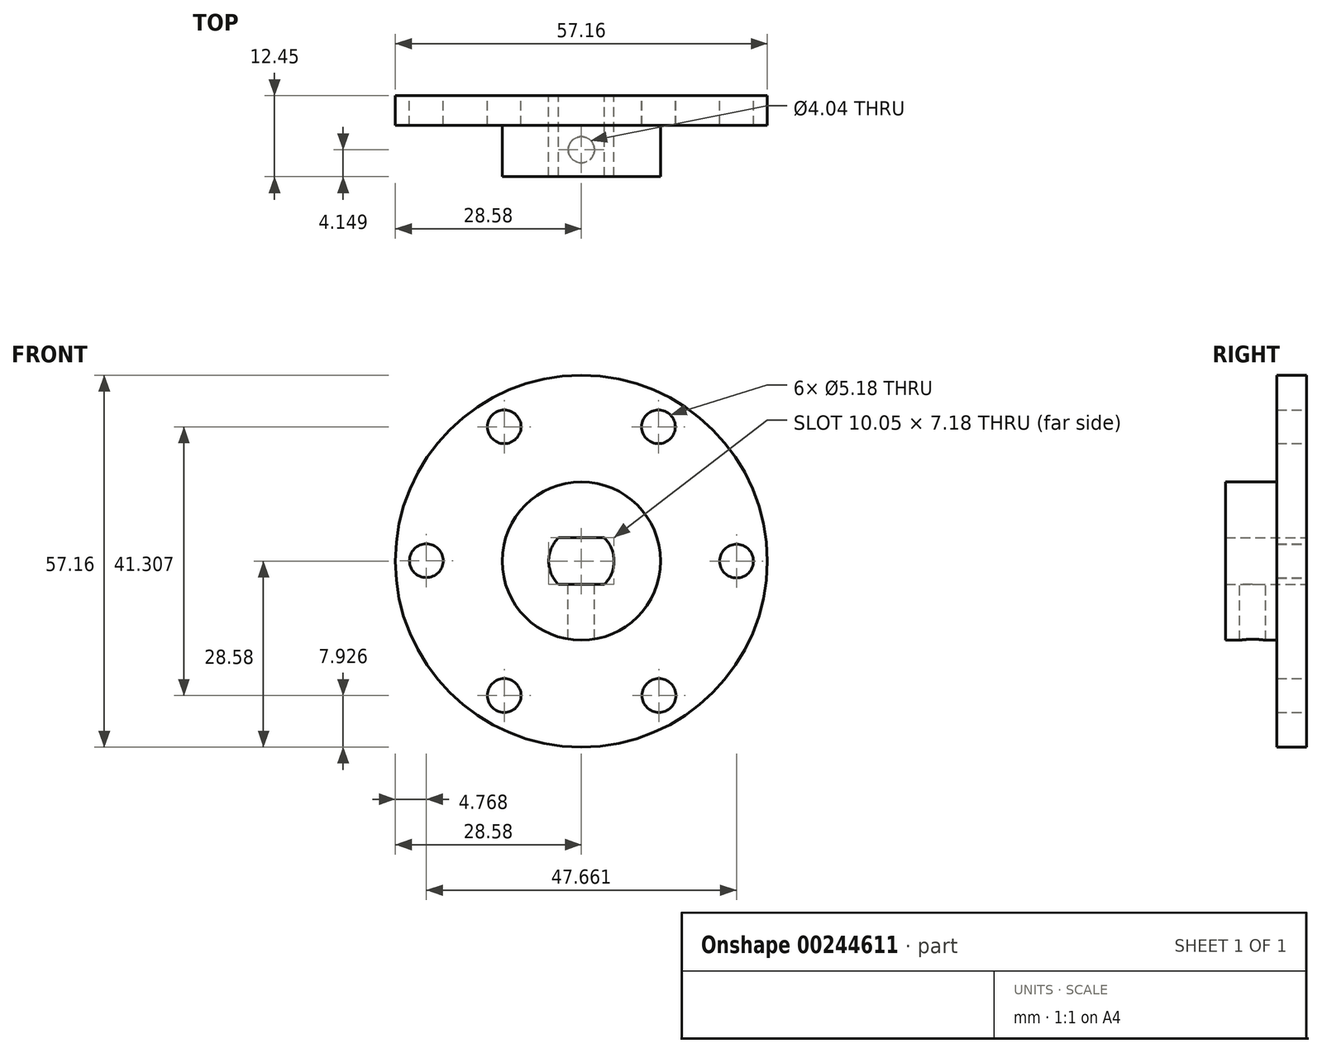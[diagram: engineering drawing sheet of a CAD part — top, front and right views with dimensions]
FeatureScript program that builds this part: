
annotation { "Feature Type Name" : "Feature", "Feature Type Description" : "" }
export const myFeature = defineFeature(function(context is Context, id is Id, definition is map)
    precondition{}
    {
        {
            var Q0;
            Q0=qCreatedBy(makeId("Front.planeOp"),FACE);
            var sketch = newSketch(context, id + "F0", { "sketchPlane" : qUnion([Q0])});
            skCircle(sketch, "E0", {"center": v(0, 0) * mm, "radius": 28.58 * mm});
            skArc(sketch, "E1", {"start": v(-11.85, 20.65) * mm, "mid": v(-11.9, 20.62) * mm, "end": v(-11.96, 20.6) * mm});
            skCircle(sketch, "E2", {"center": v(0, 0) * mm, "radius": 12.17 * mm});
            skLineSegment(sketch, "E3.0", {"start": v(-11.92, 20.65) * mm, "end": v(-11.85, 20.65) * mm});
            skLineSegment(sketch, "E3.1", {"start": v(11.92, 20.65) * mm, "end": v(11.96, 20.6) * mm});
            skLineSegment(sketch, "E3.2", {"start": v(23.85, 0) * mm, "end": v(23.81, -0.06) * mm});
            skLineSegment(sketch, "E3.3", {"start": v(11.92, -20.65) * mm, "end": v(11.85, -20.65) * mm});
            skLineSegment(sketch, "E3.4", {"start": v(-11.92, -20.65) * mm, "end": v(-11.96, -20.6) * mm});
            skLineSegment(sketch, "E3.5", {"start": v(-23.85, 0) * mm, "end": v(-23.81, 0.06) * mm});
            skPoint(sketch, "E3.0.midPoint", {"position": v(0, 20.65) * mm});
            skArc(sketch, "E4.trimOffspring", {"start": v(-23.81, 0.06) * mm, "mid": v(-23.81, 0) * mm, "end": v(-23.81, -0.06) * mm});
            skArc(sketch, "E5.trimOffspring", {"start": v(-11.96, -20.6) * mm, "mid": v(-11.9, -20.62) * mm, "end": v(-11.85, -20.65) * mm});
            skArc(sketch, "E6.trimOffspring", {"start": v(11.85, -20.65) * mm, "mid": v(11.9, -20.62) * mm, "end": v(11.96, -20.6) * mm});
            skArc(sketch, "E7.trimOffspring", {"start": v(23.81, -0.06) * mm, "mid": v(23.81, 0) * mm, "end": v(23.81, 0.06) * mm});
            skArc(sketch, "E8.trimOffspring", {"start": v(11.96, 20.6) * mm, "mid": v(11.9, 20.62) * mm, "end": v(11.85, 20.65) * mm});
            skCircle(sketch, "E9", {"center": v(-23.81, 0.06) * mm, "radius": 2.6 * mm});
            skCircle(sketch, "E10", {"center": v(-11.85, 20.65) * mm, "radius": 2.6 * mm});
            skCircle(sketch, "E11", {"center": v(11.85, 20.65) * mm, "radius": 2.6 * mm});
            skCircle(sketch, "E12", {"center": v(23.85, 0) * mm, "radius": 2.6 * mm});
            skCircle(sketch, "E13", {"center": v(11.92, -20.65) * mm, "radius": 2.6 * mm});
            skCircle(sketch, "E14", {"center": v(-11.85, -20.65) * mm, "radius": 2.6 * mm});
            skLineSegment(sketch, "E15.trimOffspring", {"start": v(11.85, 20.65) * mm, "end": v(11.92, 20.65) * mm});
            skLineSegment(sketch, "E16.trimOffspring", {"start": v(23.81, 0.06) * mm, "end": v(23.85, 0) * mm});
            skLineSegment(sketch, "E17.trimOffspring", {"start": v(11.96, -20.6) * mm, "end": v(11.92, -20.65) * mm});
            skLineSegment(sketch, "E18.trimOffspring", {"start": v(-11.85, -20.65) * mm, "end": v(-11.92, -20.65) * mm});
            skLineSegment(sketch, "E19.trimOffspring", {"start": v(-23.81, -0.06) * mm, "end": v(-23.85, 0) * mm});
            skLineSegment(sketch, "E20.trimOffspring", {"start": v(-11.96, 20.6) * mm, "end": v(-11.92, 20.65) * mm});
            skArc(sketch, "E21", {"start": v(-3.51, 3.6) * mm, "mid": v(-5.02, 0) * mm, "end": v(-3.51, -3.6) * mm});
            skLineSegment(sketch, "E22.bottom", {"start": v(3.51, 3.6) * mm, "end": v(-3.51, 3.6) * mm});
            skLineSegment(sketch, "E22.top", {"start": v(3.51, -3.6) * mm, "end": v(-3.51, -3.6) * mm});
            skArc(sketch, "E23.trimOffspring", {"start": v(3.51, -3.6) * mm, "mid": v(5.02, 0) * mm, "end": v(3.51, 3.6) * mm});
            skSolve(sketch);
        }
        {
            var Q0;
            Q0=makeQuery(id+"F0.imprint","IMPRINT",FACE,{"disambiguationData":[TD([[makeQuery(id+"F0.imprint","IMPRINT",EDGE,{"derivedFrom":sQuery(id+"F0.wireOp",EDGE,"E2")}),1.0]])]});
            extrude(context, id + "F1", {"entities" : qUnion([Q0]), "depth" : 12.45 * mm});
        }
        {
            var Q0;
            Q0=makeQuery(id+"F0.imprint","IMPRINT",FACE,{"disambiguationData":[TD([[makeQuery(id+"F0.imprint","IMPRINT",EDGE,{"derivedFrom":sQuery(id+"F0.wireOp",EDGE,"E0")}),1.0]])]});
            extrude(context, id + "F2", {"entities" : qUnion([Q0]), "operationType" : NewBodyOperationType.ADD, "depth" : 4.57 * mm});
        }
        {
            var Q0;
            Q0=qCreatedBy(makeId("Top.planeOp"),FACE);
            var sketch = newSketch(context, id + "F3", { "sketchPlane" : qUnion([Q0])});
            skCircle(sketch, "E24", {"center": v(0, -8.3) * mm, "radius": 2 * mm});
            skSolve(sketch);
        }
        {
            var Q0;
            Q0=sQuery(id+"F3.wireOp",VERTEX,"E24.center");
            var Q1;
            Q1=makeQuery(id+"F1.opExtrude","SWEPT_BODY",BODY,{"disambiguationData":[OSD([sQuery(id+"F0.wireOp",EDGE,"E2"),sQuery(id+"F0.wireOp",EDGE,"E21"),sQuery(id+"F0.wireOp",EDGE,"E22.bottom"),sQuery(id+"F0.wireOp",EDGE,"E22.top"),sQuery(id+"F0.wireOp",EDGE,"E23.trimOffspring")])]});
            hole(context, id + "F4", {"style" : HoleStyle.SIMPLE, "endStyle" : HoleEndStyle.THROUGH, "holeDiameter" : 4.04 * mm, "tappedDepth" : 12.7 * mm, "tapClearance" : 3, "locations" : qUnion([Q0]), "scope" : qUnion([Q1])});
        }
    });
